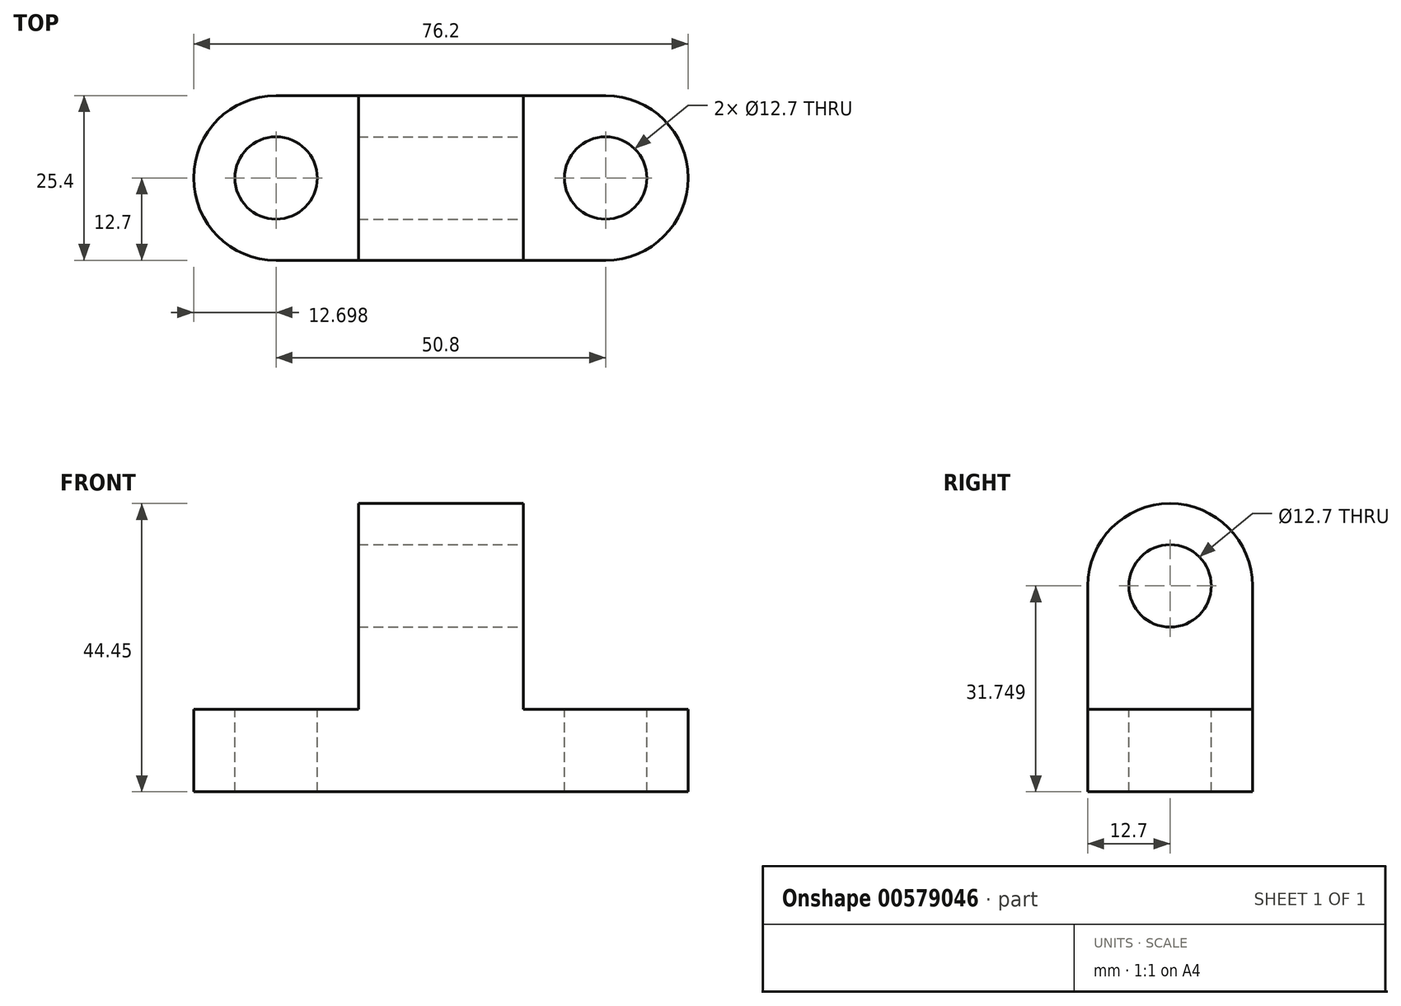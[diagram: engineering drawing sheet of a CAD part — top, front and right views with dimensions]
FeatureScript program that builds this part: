
annotation { "Feature Type Name" : "Feature", "Feature Type Description" : "" }
export const myFeature = defineFeature(function(context is Context, id is Id, definition is map)
    precondition{}
    {
        {
            var Q0;
            Q0=qCreatedBy(makeId("Front.planeOp"),FACE);
            var sketch = newSketch(context, id + "F0", { "sketchPlane" : qUnion([Q0])});
            skLineSegment(sketch, "E0", {"start": v(-67.18, 15.26) * mm, "end": v(-67.18, 2.56) * mm});
            skLineSegment(sketch, "E1", {"start": v(-67.18, 2.56) * mm, "end": v(9.02, 2.56) * mm});
            skLineSegment(sketch, "E2", {"start": v(9.02, 2.56) * mm, "end": v(9.02, 15.26) * mm});
            skLineSegment(sketch, "E3", {"start": v(9.02, 15.26) * mm, "end": v(-16.38, 15.26) * mm});
            skLineSegment(sketch, "E4", {"start": v(-16.38, 15.26) * mm, "end": v(-16.38, 47) * mm});
            skLineSegment(sketch, "E5", {"start": v(-16.38, 47) * mm, "end": v(-41.78, 47) * mm});
            skLineSegment(sketch, "E6", {"start": v(-41.78, 47) * mm, "end": v(-41.78, 15.26) * mm});
            skLineSegment(sketch, "E7", {"start": v(-41.78, 15.26) * mm, "end": v(-67.18, 15.26) * mm});
            skSolve(sketch);
        }
        {
            var Q0;
            Q0=makeQuery(id+"F0.imprint","IMPRINT",FACE,{"disambiguationData":[TD([[makeQuery(id+"F0.imprint","IMPRINT",EDGE,{"derivedFrom":sQuery(id+"F0.wireOp",EDGE,"E0")}),1.0]])]});
            extrude(context, id + "F1", {"entities" : qUnion([Q0]), "depth" : 25.4 * mm, "offsetDistance" : 25.4 * mm});
        }
        {
            var Q0;
            Q0=makeQuery(id+"F1.opExtrude","SWEPT_FACE",FACE,{"disambiguationData":[OSD([sQuery(id+"F0.wireOp",EDGE,"E3")])]});
            var sketch = newSketch(context, id + "F2", { "sketchPlane" : qUnion([Q0])});
            skCircle(sketch, "E8", {"center": v(-3.68, -12.7) * mm, "radius": 6.35 * mm});
            skCircle(sketch, "E9", {"center": v(-54.48, -12.7) * mm, "radius": 6.35 * mm});
            skSolve(sketch);
        }
        {
            var Q0;
            Q0=makeQuery(id+"F2.imprint","IMPRINT",FACE,{"disambiguationData":[TD([[makeQuery(id+"F2.imprint","IMPRINT",EDGE,{"derivedFrom":sQuery(id+"F2.wireOp",EDGE,"E9")}),1.0]])]});
            var Q1;
            Q1=makeQuery(id+"F2.imprint","IMPRINT",FACE,{"disambiguationData":[TD([[makeQuery(id+"F2.imprint","IMPRINT",EDGE,{"derivedFrom":sQuery(id+"F2.wireOp",EDGE,"E8")}),1.0]])]});
            extrude(context, id + "F3", {"entities" : qUnion([Q0, Q1]), "operationType" : NewBodyOperationType.REMOVE, "endBound" : BoundingType.THROUGH_ALL, "oppositeDirection" : true, "depth" : 25.4 * mm, "offsetDistance" : 25.4 * mm});
        }
        {
            var Q0;
            Q0=makeQuery(id+"F1.opExtrude","SWEPT_FACE",FACE,{"disambiguationData":[OSD([sQuery(id+"F0.wireOp",EDGE,"E4")])]});
            var sketch = newSketch(context, id + "F4", { "sketchPlane" : qUnion([Q0])});
            skCircle(sketch, "E10", {"center": v(-12.7, 34.3) * mm, "radius": 12.7 * mm});
            skSolve(sketch);
        }
        {
            var Q0;
            {var subQ0=sQuery(id+"F4.wireOp",EDGE,"E10");var subQ1=sQuery(id+"F0.wireOp",EDGE,"E4");var subQ4=makeQuery(id+"F1.opExtrude","CAP_EDGE",EDGE,{"disambiguationData":[OSD([subQ1])],"isStart":false});var subQ5=makeQuery(id+"F4.imprint","INTERSECT",VERTEX,{"derivedFrom":[subQ4,subQ0]});Q0=makeQuery(id+"F4.imprint","IMPRINT",FACE,{"disambiguationData":[TD([[makeQuery(id+"F4.imprint","IMPRINT",EDGE,{"disambiguationData":[TD([[subQ5,1.0]])],"derivedFrom":subQ0}),-1.0]])]});}
            var Q1;
            {var subQ0=sQuery(id+"F4.wireOp",EDGE,"E10");var subQ1=sQuery(id+"F0.wireOp",EDGE,"E4");var subQ4=makeQuery(id+"F1.opExtrude","CAP_EDGE",EDGE,{"disambiguationData":[OSD([subQ1])],"isStart":true});var subQ5=makeQuery(id+"F4.imprint","INTERSECT",VERTEX,{"derivedFrom":[subQ4,subQ0]});Q1=makeQuery(id+"F4.imprint","IMPRINT",FACE,{"disambiguationData":[TD([[makeQuery(id+"F4.imprint","IMPRINT",EDGE,{"disambiguationData":[TD([[subQ5,-1.0]])],"derivedFrom":subQ0}),-1.0]])]});}
            extrude(context, id + "F5", {"entities" : qUnion([Q0, Q1]), "operationType" : NewBodyOperationType.REMOVE, "endBound" : BoundingType.THROUGH_ALL, "oppositeDirection" : true, "depth" : 25.4 * mm, "offsetDistance" : 25.4 * mm});
        }
        {
            var Q0;
            Q0=makeQuery(id+"F1.opExtrude","SWEPT_FACE",FACE,{"disambiguationData":[OSD([sQuery(id+"F0.wireOp",EDGE,"E4")])]});
            var sketch = newSketch(context, id + "F6", { "sketchPlane" : qUnion([Q0])});
            skCircle(sketch, "E11", {"center": v(-12.7, 34.3) * mm, "radius": 6.35 * mm});
            skSolve(sketch);
        }
        {
            var Q0;
            Q0=makeQuery(id+"F6.imprint","IMPRINT",FACE,{"disambiguationData":[TD([[makeQuery(id+"F6.imprint","IMPRINT",EDGE,{"derivedFrom":sQuery(id+"F6.wireOp",EDGE,"E11")}),1.0]])]});
            extrude(context, id + "F7", {"entities" : qUnion([Q0]), "operationType" : NewBodyOperationType.REMOVE, "endBound" : BoundingType.THROUGH_ALL, "oppositeDirection" : true, "depth" : 25.4 * mm, "offsetDistance" : 25.4 * mm});
        }
        {
            var Q0;
            Q0=makeQuery(id+"F1.opExtrude","SWEPT_FACE",FACE,{"disambiguationData":[OSD([sQuery(id+"F0.wireOp",EDGE,"E3")])]});
            var sketch = newSketch(context, id + "F8", { "sketchPlane" : qUnion([Q0])});
            skCircle(sketch, "E12", {"center": v(-3.68, -12.7) * mm, "radius": 12.7 * mm});
            skSolve(sketch);
        }
        {
            var Q0;
            {var subQ0=sQuery(id+"F8.wireOp",EDGE,"E12");var subQ1=sQuery(id+"F0.wireOp",EDGE,"E3");var subQ2=makeQuery(id+"F1.opExtrude","CAP_EDGE",EDGE,{"disambiguationData":[OSD([subQ1])],"isStart":true});var subQ3=makeQuery(id+"F8.imprint","INTERSECT",VERTEX,{"derivedFrom":[subQ2,subQ0]});Q0=makeQuery(id+"F8.imprint","IMPRINT",FACE,{"disambiguationData":[TD([[makeQuery(id+"F8.imprint","IMPRINT",EDGE,{"disambiguationData":[TD([[subQ3,1.0]])],"derivedFrom":subQ0}),-1.0]])]});}
            var Q1;
            {var subQ0=sQuery(id+"F8.wireOp",EDGE,"E12");var subQ1=sQuery(id+"F0.wireOp",EDGE,"E3");var subQ4=makeQuery(id+"F1.opExtrude","CAP_EDGE",EDGE,{"disambiguationData":[OSD([subQ1])],"isStart":false});var subQ5=makeQuery(id+"F8.imprint","INTERSECT",VERTEX,{"derivedFrom":[subQ4,subQ0]});Q1=makeQuery(id+"F8.imprint","IMPRINT",FACE,{"disambiguationData":[TD([[makeQuery(id+"F8.imprint","IMPRINT",EDGE,{"disambiguationData":[TD([[subQ5,-1.0]])],"derivedFrom":subQ0}),-1.0]])]});}
            extrude(context, id + "F9", {"entities" : qUnion([Q0, Q1]), "operationType" : NewBodyOperationType.REMOVE, "endBound" : BoundingType.THROUGH_ALL, "oppositeDirection" : true, "depth" : 25.4 * mm, "offsetDistance" : 25.4 * mm});
        }
        {
            var Q0;
            Q0=makeQuery(id+"F1.opExtrude","SWEPT_FACE",FACE,{"disambiguationData":[OSD([sQuery(id+"F0.wireOp",EDGE,"E7")])]});
            var sketch = newSketch(context, id + "F10", { "sketchPlane" : qUnion([Q0])});
            skCircle(sketch, "E13", {"center": v(-54.48, -12.7) * mm, "radius": 12.7 * mm});
            skSolve(sketch);
        }
        {
            var Q0;
            {var subQ0=sQuery(id+"F10.wireOp",EDGE,"E13");var subQ1=sQuery(id+"F0.wireOp",EDGE,"E7");var subQ2=makeQuery(id+"F1.opExtrude","CAP_EDGE",EDGE,{"disambiguationData":[OSD([subQ1])],"isStart":true});var subQ3=makeQuery(id+"F10.imprint","INTERSECT",VERTEX,{"derivedFrom":[subQ2,subQ0]});Q0=makeQuery(id+"F10.imprint","IMPRINT",FACE,{"disambiguationData":[TD([[makeQuery(id+"F10.imprint","IMPRINT",EDGE,{"disambiguationData":[TD([[subQ3,-1.0]])],"derivedFrom":subQ0}),-1.0]])]});}
            var Q1;
            {var subQ0=sQuery(id+"F10.wireOp",EDGE,"E13");var subQ1=sQuery(id+"F0.wireOp",EDGE,"E7");var subQ4=makeQuery(id+"F1.opExtrude","CAP_EDGE",EDGE,{"disambiguationData":[OSD([subQ1])],"isStart":false});var subQ5=makeQuery(id+"F10.imprint","INTERSECT",VERTEX,{"derivedFrom":[subQ4,subQ0]});Q1=makeQuery(id+"F10.imprint","IMPRINT",FACE,{"disambiguationData":[TD([[makeQuery(id+"F10.imprint","IMPRINT",EDGE,{"disambiguationData":[TD([[subQ5,1.0]])],"derivedFrom":subQ0}),-1.0]])]});}
            extrude(context, id + "F11", {"entities" : qUnion([Q0, Q1]), "operationType" : NewBodyOperationType.REMOVE, "endBound" : BoundingType.THROUGH_ALL, "oppositeDirection" : true, "depth" : 25.4 * mm, "offsetDistance" : 25.4 * mm});
        }
    });
